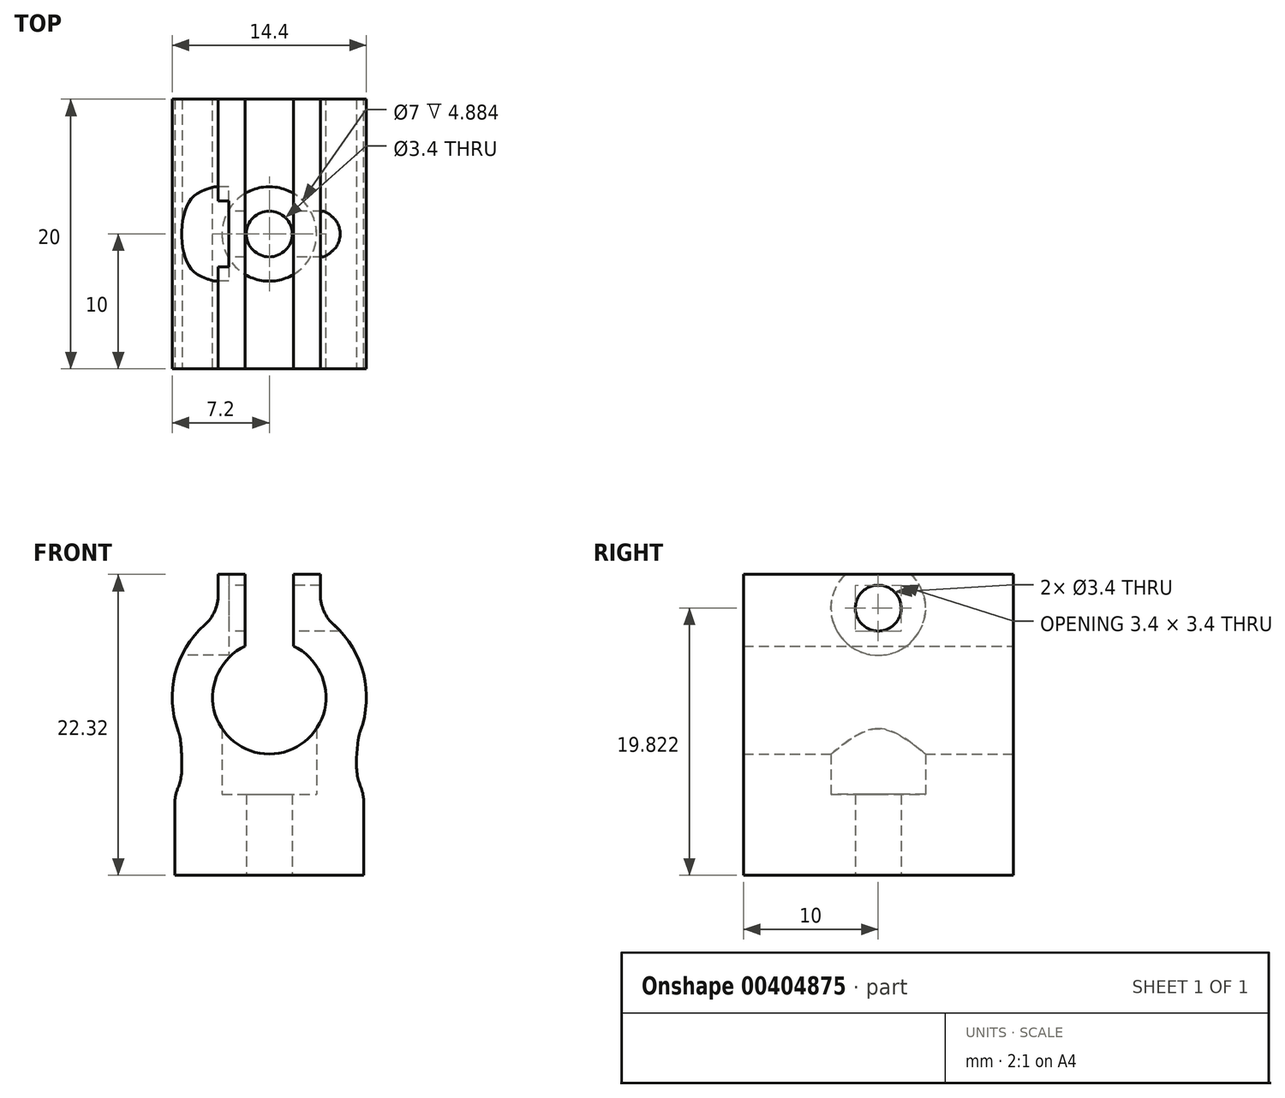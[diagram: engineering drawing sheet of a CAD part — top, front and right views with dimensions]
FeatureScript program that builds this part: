
annotation { "Feature Type Name" : "Feature", "Feature Type Description" : "" }
export const myFeature = defineFeature(function(context is Context, id is Id, definition is map)
    precondition{}
    {
        {
            var Q0;
            Q0=qCreatedBy(makeId("Front.planeOp"),FACE);
            var sketch = newSketch(context, id + "F0", { "sketchPlane" : qUnion([Q0])});
            skArc(sketch, "E0", {"start": v(-1.79, 3.8) * mm, "mid": v(0, -4.2) * mm, "end": v(1.79, 3.8) * mm});
            skArc(sketch, "E1", {"start": v(-3.79, 6.12) * mm, "mid": v(-6.86, 2.19) * mm, "end": v(-6.64, -2.8) * mm});
            skLineSegment(sketch, "E2", {"start": v(3.79, 9.12) * mm, "end": v(3.79, 6.12) * mm});
            skLineSegment(sketch, "E3", {"start": v(-1.79, 9.12) * mm, "end": v(-1.79, 3.8) * mm});
            skLineSegment(sketch, "E4", {"start": v(1.79, 9.12) * mm, "end": v(1.79, 3.8) * mm});
            skLineSegment(sketch, "E5", {"start": v(-1.79, 9.12) * mm, "end": v(-3.79, 9.12) * mm});
            skLineSegment(sketch, "E6", {"start": v(-3.79, 6.12) * mm, "end": v(-3.79, 9.12) * mm});
            skLineSegment(sketch, "E7", {"start": v(1.79, 9.12) * mm, "end": v(3.79, 9.12) * mm});
            skLineSegment(sketch, "E8", {"start": v(-7, -7.2) * mm, "end": v(-7, -13.2) * mm});
            skLineSegment(sketch, "E9", {"start": v(-7, -13.2) * mm, "end": v(7, -13.2) * mm});
            skLineSegment(sketch, "E10", {"start": v(7, -7.2) * mm, "end": v(7, -13.2) * mm});
            skPoint(sketch, "E11.orphan", {"position": v(9.08, -13.2) * mm});
            skFitSpline(sketch, "E12", {"points": [v(-7, -7.2) * mm, v(-6.5, -5.54) * mm, v(-6.64, -2.8) * mm, v(-6.64, -2.77) * mm], "startDerivative": vector(1.57, 3.06) * mm, "endDerivative": vector(-0.17, 0.18) * mm});
            skFitSpline(sketch, "E13", {"points": [v(7, -7.2) * mm, v(6.5, -5.54) * mm, v(6.64, -2.8) * mm], "startDerivative": vector(-1.44, 3.48) * mm, "endDerivative": vector(0.64, 5.26) * mm});
            skArc(sketch, "E14.trimOffspring", {"start": v(6.64, -2.8) * mm, "mid": v(6.86, 2.19) * mm, "end": v(3.79, 6.12) * mm});
            skSolve(sketch);
        }
        {
            var Q0;
            Q0=qSketchRegion(id+"F0",true);
            extrude(context, id + "F1", {"entities" : qUnion([Q0]), "depth" : 20 * mm});
        }
        {
            var Q0;
            Q0=makeQuery(id+"F1.opExtrude","SWEPT_FACE",FACE,{"disambiguationData":[OSD([sQuery(id+"F0.wireOp",EDGE,"E8")])]});
            var sketch = newSketch(context, id + "F2", { "sketchPlane" : qUnion([Q0])});
            skLineSegment(sketch, "E15", {"start": v(10, -13.2) * mm, "end": v(10, 6.62) * mm, "construction": true});
            skCircle(sketch, "E16", {"center": v(10, 6.62) * mm, "radius": 1.7 * mm});
            skCircle(sketch, "E17", {"center": v(10, 6.62) * mm, "radius": 3.5 * mm});
            skSolve(sketch);
        }
        {
            var Q0;
            Q0=makeQuery(id+"F2.imprint","IMPRINT",FACE,{"disambiguationData":[TD([[makeQuery(id+"F2.imprint","IMPRINT",EDGE,{"derivedFrom":sQuery(id+"F2.wireOp",EDGE,"E16")}),-1.0]])]});
            extrude(context, id + "F3", {"entities" : qUnion([Q0]), "operationType" : NewBodyOperationType.REMOVE, "oppositeDirection" : true, "depth" : 4 * mm});
        }
        {
            var Q0;
            Q0=makeQuery(id+"F2.imprint","IMPRINT",FACE,{"disambiguationData":[TD([[makeQuery(id+"F2.imprint","IMPRINT",EDGE,{"derivedFrom":sQuery(id+"F2.wireOp",EDGE,"E16")}),1.0]])]});
            extrude(context, id + "F4", {"entities" : qUnion([Q0]), "operationType" : NewBodyOperationType.REMOVE, "oppositeDirection" : true, "depth" : 25 * mm});
        }
        {
            var Q0;
            Q0=makeQuery(id+"F1.opExtrude","SWEPT_EDGE",EDGE,{"disambiguationData":[OSD([sQuery(id+"F0.wireOp",EDGE,"E1"),sQuery(id+"F0.wireOp",EDGE,"E12")])]});
            var Q1;
            Q1=makeQuery(id+"F1.opExtrude","SWEPT_EDGE",EDGE,{"disambiguationData":[OSD([sQuery(id+"F0.wireOp",EDGE,"E13"),sQuery(id+"F0.wireOp",EDGE,"E14.trimOffspring")])]});
            var Q2;
            Q2=makeQuery(id+"F1.opExtrude","SWEPT_EDGE",EDGE,{"disambiguationData":[OSD([sQuery(id+"F0.wireOp",EDGE,"E8"),sQuery(id+"F0.wireOp",EDGE,"E12")])]});
            var Q3;
            Q3=makeQuery(id+"F1.opExtrude","SWEPT_EDGE",EDGE,{"disambiguationData":[OSD([sQuery(id+"F0.wireOp",EDGE,"E10"),sQuery(id+"F0.wireOp",EDGE,"E13")])]});
            var Q4;
            {var subQ0=sQuery(id+"F0.wireOp",EDGE,"E14.trimOffspring");var subQ1=sQuery(id+"F0.wireOp",EDGE,"E2");Q4=makeQuery(id+"F4.boolean.opBoolean","SPLIT",EDGE,{"disambiguationData":[TD([makeQuery(id+"F1.opExtrude","CAP_FACE",FACE,{"disambiguationData":[OSD([sQuery(id+"F0.wireOp",EDGE,"E0"),sQuery(id+"F0.wireOp",EDGE,"E1"),subQ1,sQuery(id+"F0.wireOp",EDGE,"E3"),sQuery(id+"F0.wireOp",EDGE,"E4"),sQuery(id+"F0.wireOp",EDGE,"E5"),sQuery(id+"F0.wireOp",EDGE,"E6"),sQuery(id+"F0.wireOp",EDGE,"E7"),sQuery(id+"F0.wireOp",EDGE,"E8"),sQuery(id+"F0.wireOp",EDGE,"E9"),sQuery(id+"F0.wireOp",EDGE,"E10"),sQuery(id+"F0.wireOp",EDGE,"E12"),sQuery(id+"F0.wireOp",EDGE,"E13"),subQ0])],"isStart":false})])],"derivedFrom":makeQuery(id+"F1.opExtrude","SWEPT_EDGE",EDGE,{"disambiguationData":[OSD([subQ1,subQ0])]})});}
            var Q5;
            {var subQ0=sQuery(id+"F0.wireOp",EDGE,"E14.trimOffspring");var subQ1=sQuery(id+"F0.wireOp",EDGE,"E2");Q5=makeQuery(id+"F4.boolean.opBoolean","SPLIT",EDGE,{"disambiguationData":[TD([makeQuery(id+"F1.opExtrude","CAP_FACE",FACE,{"disambiguationData":[OSD([sQuery(id+"F0.wireOp",EDGE,"E0"),sQuery(id+"F0.wireOp",EDGE,"E1"),subQ1,sQuery(id+"F0.wireOp",EDGE,"E3"),sQuery(id+"F0.wireOp",EDGE,"E4"),sQuery(id+"F0.wireOp",EDGE,"E5"),sQuery(id+"F0.wireOp",EDGE,"E6"),sQuery(id+"F0.wireOp",EDGE,"E7"),sQuery(id+"F0.wireOp",EDGE,"E8"),sQuery(id+"F0.wireOp",EDGE,"E9"),sQuery(id+"F0.wireOp",EDGE,"E10"),sQuery(id+"F0.wireOp",EDGE,"E12"),sQuery(id+"F0.wireOp",EDGE,"E13"),subQ0])],"isStart":true})])],"derivedFrom":makeQuery(id+"F1.opExtrude","SWEPT_EDGE",EDGE,{"disambiguationData":[OSD([subQ1,subQ0])]})});}
            var Q6;
            {var subQ0=sQuery(id+"F0.wireOp",EDGE,"E6");var subQ1=sQuery(id+"F0.wireOp",EDGE,"E1");Q6=makeQuery(id+"F3.boolean.opBoolean","SPLIT",EDGE,{"disambiguationData":[TD([makeQuery(id+"F1.opExtrude","CAP_FACE",FACE,{"disambiguationData":[OSD([sQuery(id+"F0.wireOp",EDGE,"E0"),subQ1,sQuery(id+"F0.wireOp",EDGE,"E2"),sQuery(id+"F0.wireOp",EDGE,"E3"),sQuery(id+"F0.wireOp",EDGE,"E4"),sQuery(id+"F0.wireOp",EDGE,"E5"),subQ0,sQuery(id+"F0.wireOp",EDGE,"E7"),sQuery(id+"F0.wireOp",EDGE,"E8"),sQuery(id+"F0.wireOp",EDGE,"E9"),sQuery(id+"F0.wireOp",EDGE,"E10"),sQuery(id+"F0.wireOp",EDGE,"E12"),sQuery(id+"F0.wireOp",EDGE,"E13"),sQuery(id+"F0.wireOp",EDGE,"E14.trimOffspring")])],"isStart":true})])],"derivedFrom":makeQuery(id+"F1.opExtrude","SWEPT_EDGE",EDGE,{"disambiguationData":[OSD([subQ1,subQ0])]})});}
            var Q7;
            {var subQ0=sQuery(id+"F0.wireOp",EDGE,"E6");var subQ1=sQuery(id+"F0.wireOp",EDGE,"E1");Q7=makeQuery(id+"F3.boolean.opBoolean","SPLIT",EDGE,{"disambiguationData":[TD([makeQuery(id+"F1.opExtrude","CAP_FACE",FACE,{"disambiguationData":[OSD([sQuery(id+"F0.wireOp",EDGE,"E0"),subQ1,sQuery(id+"F0.wireOp",EDGE,"E2"),sQuery(id+"F0.wireOp",EDGE,"E3"),sQuery(id+"F0.wireOp",EDGE,"E4"),sQuery(id+"F0.wireOp",EDGE,"E5"),subQ0,sQuery(id+"F0.wireOp",EDGE,"E7"),sQuery(id+"F0.wireOp",EDGE,"E8"),sQuery(id+"F0.wireOp",EDGE,"E9"),sQuery(id+"F0.wireOp",EDGE,"E10"),sQuery(id+"F0.wireOp",EDGE,"E12"),sQuery(id+"F0.wireOp",EDGE,"E13"),sQuery(id+"F0.wireOp",EDGE,"E14.trimOffspring")])],"isStart":false})])],"derivedFrom":makeQuery(id+"F1.opExtrude","SWEPT_EDGE",EDGE,{"disambiguationData":[OSD([subQ1,subQ0])]})});}
            fillet(context, id + "F5", {"entities" : qUnion([Q0, Q1, Q2, Q3, Q4, Q5, Q6, Q7]), "radius" : 3 * mm, "tangentPropagation" : true, "allowEdgeOverflow" : false});
        }
        {
            var Q0;
            Q0=makeQuery(id+"F1.opExtrude","SWEPT_FACE",FACE,{"disambiguationData":[OSD([sQuery(id+"F0.wireOp",EDGE,"E9")])]});
            var sketch = newSketch(context, id + "F6", { "sketchPlane" : qUnion([Q0])});
            skLineSegment(sketch, "E18", {"start": v(-7, 10) * mm, "end": v(0, 10) * mm, "construction": true});
            skCircle(sketch, "E19", {"center": v(0, 10) * mm, "radius": 1.7 * mm});
            skCircle(sketch, "E20", {"center": v(0, 10) * mm, "radius": 3.5 * mm});
            skSolve(sketch);
        }
        {
            var Q0;
            Q0=makeQuery(id+"F6.imprint","IMPRINT",FACE,{"disambiguationData":[TD([[makeQuery(id+"F6.imprint","IMPRINT",EDGE,{"derivedFrom":sQuery(id+"F6.wireOp",EDGE,"E19")}),-1.0]])]});
            extrude(context, id + "F7", {"entities" : qUnion([Q0]), "operationType" : NewBodyOperationType.REMOVE, "oppositeDirection" : true, "depth" : 12 * mm});
        }
        {
            var Q0;
            Q0=makeQuery(id+"F7.boolean.opBoolean","SPLIT",FACE,{"disambiguationData":[TD([makeQuery(id+"F7.opExtrude","SWEPT_FACE",FACE,{"disambiguationData":[OSD([sQuery(id+"F6.wireOp",EDGE,"E19")])]})])],"derivedFrom":makeQuery(id+"F1.opExtrude","SWEPT_FACE",FACE,{"disambiguationData":[OSD([sQuery(id+"F0.wireOp",EDGE,"E9")])]})});
            extrude(context, id + "F8", {"entities" : qUnion([Q0]), "operationType" : NewBodyOperationType.REMOVE, "oppositeDirection" : true, "depth" : 12 * mm});
        }
        {
            var Q0;
            Q0=makeQuery(id+"F6.imprint","IMPRINT",FACE,{"disambiguationData":[TD([[makeQuery(id+"F6.imprint","IMPRINT",EDGE,{"derivedFrom":sQuery(id+"F6.wireOp",EDGE,"E19")}),-1.0]])]});
            extrude(context, id + "F9", {"entities" : qUnion([Q0]), "operationType" : NewBodyOperationType.ADD, "oppositeDirection" : true, "depth" : 6 * mm});
        }
    });
